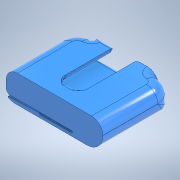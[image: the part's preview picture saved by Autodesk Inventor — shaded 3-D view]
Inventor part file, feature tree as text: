
AUTODESK INVENTOR PART (.ipt)
format: ipt  version: 2022 (Build 260153000, 153)  size: 880,128 bytes
history: native  units: mm
features: fillet x22, extrude x14, sketch x14, other x3, chamfer x2, mirror x1
ambient origin geometry x8: Origin, YZ Plane, XZ Plane, XY Plane, X Axis, Y Axis, Z Axis, Center Point
bodies: Body1 (feature_tree), Body2 (feature_tree), Body3 (feature_tree)
feature tree (56):
  other  "Popsocket"
  extrude  "Extrusion1"  Depth=1.26mm TaperAngle=0.0deg
  extrude  "Extrusion2"  Depth=3.5mm
  extrude  "Extrusion3"  Depth=4.26mm TaperAngle=0.0deg
  fillet  "Fillet1"  Radius=5.0mm
  extrude  "Extrusion4"  Depth=4.3mm TaperAngle=0.0deg
  extrude  "Extrusion5"  Depth=2.0mm TaperAngle=0.0deg
  fillet  "Fillet4"  Radius=150.0mm
  fillet  "Fillet5"  Radius=71.0mm
  chamfer  "Chamfer1"  Distance=10.0mm
  fillet  "Fillet6"  Radius=5.0mm
  extrude  "Extrusion6"  Depth=1.0mm
  fillet  "Fillet2"  Radius=1.0mm
  fillet  "Fillet3"  Radius=0.2mm
  extrude  "Extrusion12"  Depth=30.0mm
  extrude  "Extrusion13"  Depth=22.0mm
  extrude  "Extrusion14"  Depth=9.0mm
  extrude  "Extrusion15"  Depth=0.1mm
  chamfer  "Chamfer2"  Distance=9.75mm
  fillet  "Fillet9"  Radius=9.75mm
  fillet  "Fillet10"  Radius=14.0mm
  fillet  "Fillet11"  Radius=9.25mm
  fillet  "Fillet12"  Radius=1.82mm
  fillet  "Fillet13"  Radius=1.26mm
  extrude  "Extrusion16"  Depth=5.5mm
  fillet  "Fillet14"  Radius=4.0mm
  mirror  "Mirror1"
  extrude  "Extrusion17"  Depth=1.7mm
  extrude  "Extrusion18"  Depth=10.0mm TaperAngle=0.0deg
  extrude  "Extrusion19"  Depth=1.0mm TaperAngle=45.0deg
  fillet  "Fillet16"  Radius=2.0mm
  fillet  "Fillet17"  Radius=10.0mm
  fillet  "Fillet18"  Radius=7.0mm
  fillet  "Fillet19"  Radius=2.0mm
  fillet  "Fillet20"  Radius=4.0mm
  fillet  "Fillet21"  Radius=7.0mm
  fillet  "Fillet22"  Radius=1.5mm
  fillet  "Fillet23"  Radius=6.0mm
  fillet  "Fillet24"  Radius=19.0mm
  fillet  "Fillet25"  Radius=41.0mm
  sketch  "Sketch1"  dims[d0=39.99mm d1=1.26mm d2=0.0mm]
  sketch  "Sketch2"  dims[d3=35.5mm d4=3.5mm d5=0.349066mm]
  sketch  "Sketch3"  dims[d6=22.0mm d7=4.26mm d8=0.0mm d9=5.0mm]
  sketch  "Sketch4"  dims[d10=14.43mm d11=4.3mm d12=0.0mm]
  sketch  "Sketch5"  dims[d13=36.7mm d14=2.0mm d15=0.0mm d16=150.0mm d17=71.0mm]
  sketch  "Sketch6"  dims[d18=75.0mm]
  other  "Phone"
  sketch  "Sketch13"  dims[d19=35.5mm d20=10.0mm d21=0.0mm d22=5.0mm]
  other  "HolsterV2"
  sketch  "Sketch14"  dims[d23=4.9mm d24=1.0mm d25=1.0mm]
  sketch  "Sketch15"  dims[d26=1.0mm d27=2.0mm d28=60.0deg d29=0.2mm]
  sketch  "Sketch16"  dims[d60=30.0mm d61=30.0mm]
  sketch  "Sketch17"  dims[d62=22.0mm d63=22.0mm]
  sketch  "Sketch18"  dims[d64=3.0mm d65=0.0mm d66=9.0mm]
  sketch  "Sketch19"  dims[d67=9.0mm d68=0.1mm d69=9.75mm d70=0.0mm d71=9.75mm d72=0.0mm d73=14.0mm d74=9.25mm d75=1.82mm d76=1.26mm]
  sketch  "Sketch21"  dims[d77=2.1mm d78=5.5mm d79=4.0mm d80=1.7mm d81=10.0mm d82=0.0mm d83=1.0mm d84=2.0mm d85=45.0deg d86=2.0mm d87=10.0mm d88=7.0mm d89=2.0mm d90=4.0mm d92=7.0mm d93=1.5mm d94=0.0mm d95=6.0mm d97=19.0mm d98=41.0mm d99=1.0mm d100=0.0mm d101=2.0mm d102=0.0mm d103=20.4mm d104=0.7mm d105=2.0mm d106=0.0mm d107=10.0mm d108=10.0mm d109=0.5mm d110=2.0mm d111=2.0mm d112=2.0mm d113=0.2mm d114=25.25mm d115=0.9mm d116=3.0mm d117=0.2mm d35=0.5mm d36=0.872665mm d37=0.5mm d38=0.872665mm]
